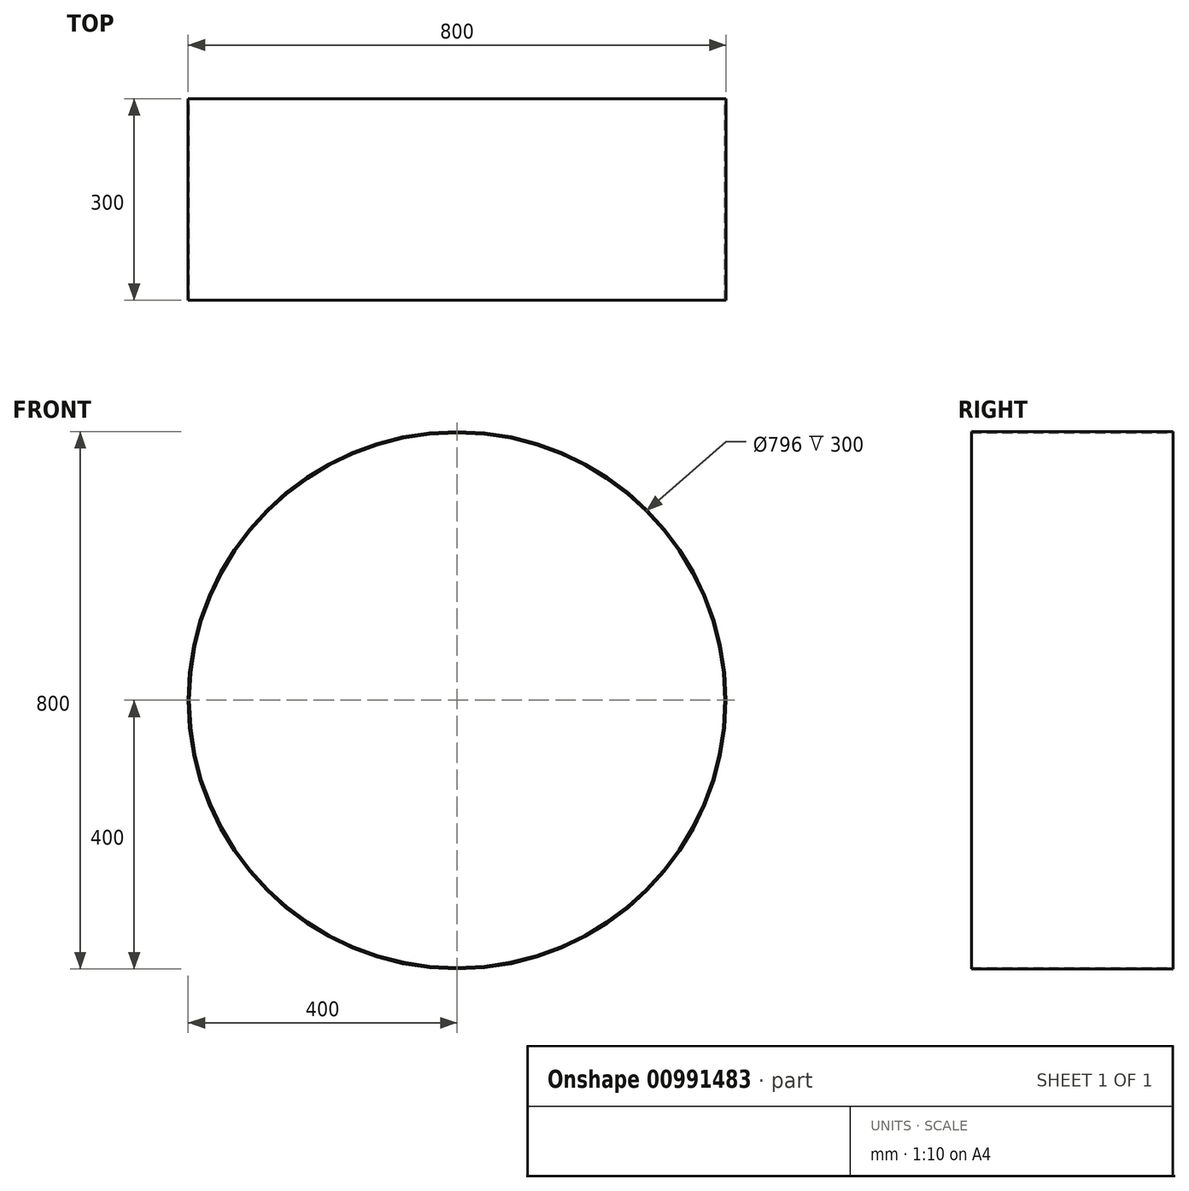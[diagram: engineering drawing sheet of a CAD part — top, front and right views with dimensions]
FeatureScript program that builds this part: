
annotation { "Feature Type Name" : "Feature", "Feature Type Description" : "" }
export const myFeature = defineFeature(function(context is Context, id is Id, definition is map)
    precondition{}
    {
        {
            var Q0;
            Q0=qCreatedBy(makeId("Front.planeOp"),FACE);
            var sketch = newSketch(context, id + "F0", { "sketchPlane" : qUnion([Q0])});
            skCircle(sketch, "E0", {"center": v(0, 0) * mm, "radius": 400 * mm});
            skCircle(sketch, "E1", {"center": v(0, 0) * mm, "radius": 398 * mm});
            skSolve(sketch);
        }
        {
            var Q0;
            Q0 = qSketchRegion(id + "F0", true);
            extrude(context, id + "F1", {"entities" : qUnion([Q0]), "depth" : 300 * mm, "offsetDistance" : 25 * mm});
        }
    });
